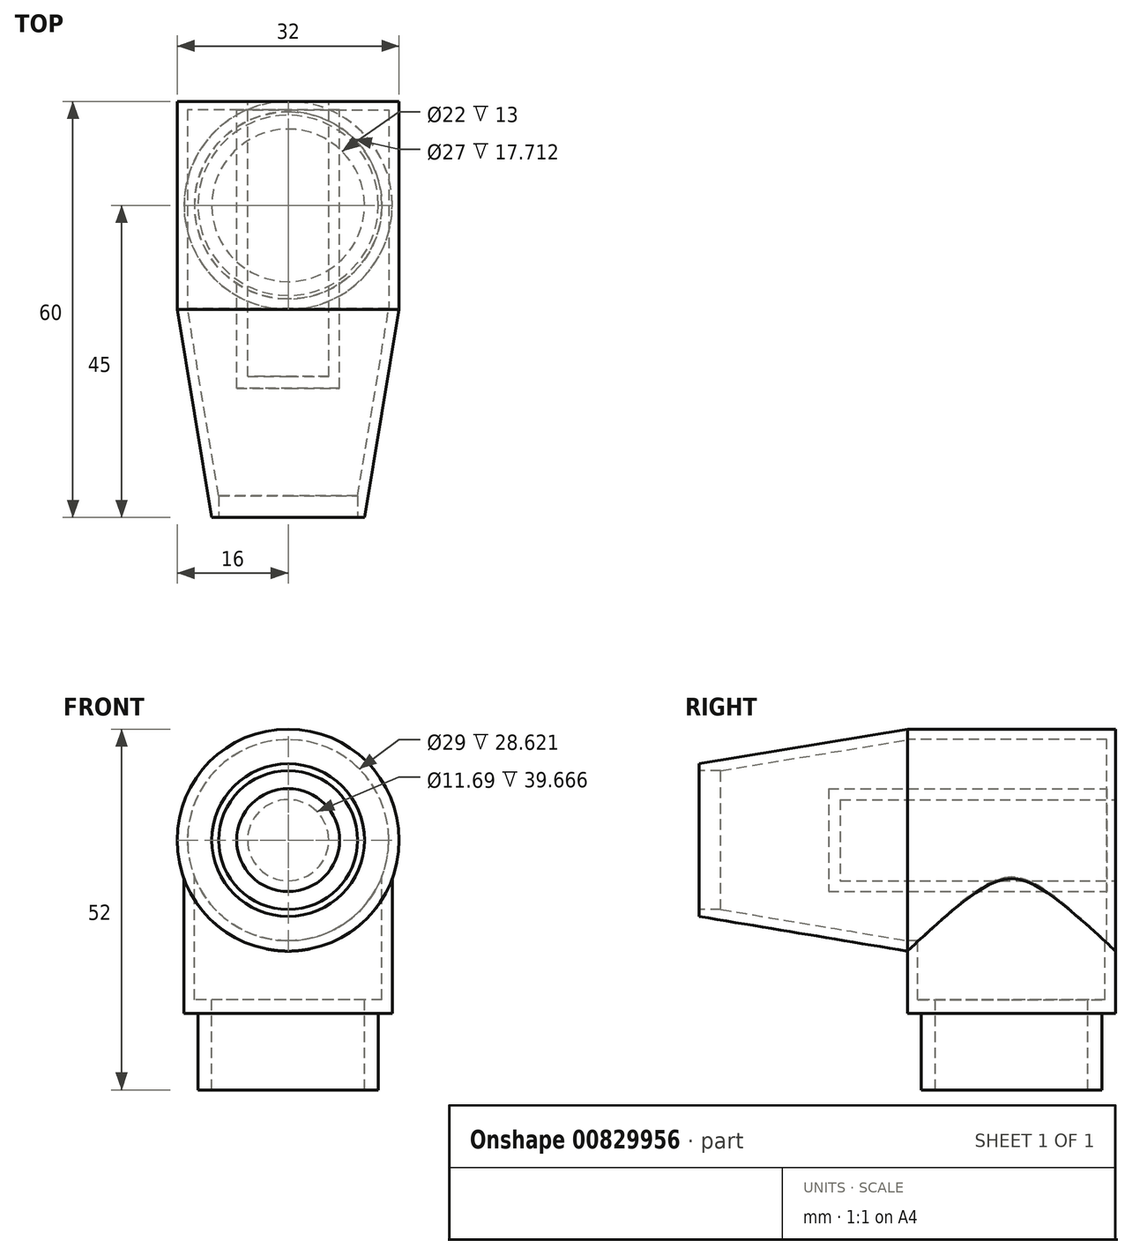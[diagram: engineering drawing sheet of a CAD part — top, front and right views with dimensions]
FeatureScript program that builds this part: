
annotation { "Feature Type Name" : "Feature", "Feature Type Description" : "" }
export const myFeature = defineFeature(function(context is Context, id is Id, definition is map)
    precondition{}
    {
        {
            var Q0;
            Q0=qCreatedBy(makeId("Right.planeOp"),FACE);
            var sketch = newSketch(context, id + "F0", { "sketchPlane" : qUnion([Q0])});
            skLineSegment(sketch, "E0", {"start": v(-38.09, 0) * mm, "end": v(40.8, 0) * mm, "construction": true});
            skLineSegment(sketch, "E1", {"start": v(0.12, 14.5) * mm, "end": v(30, 14.5) * mm});
            skLineSegment(sketch, "E2", {"start": v(30, 14.5) * mm, "end": v(30, 16) * mm});
            skLineSegment(sketch, "E3", {"start": v(30, 16) * mm, "end": v(0, 16) * mm});
            skLineSegment(sketch, "E4", {"start": v(0, 16) * mm, "end": v(-30, 11) * mm});
            skLineSegment(sketch, "E5", {"start": v(-30, 11) * mm, "end": v(-30, 10) * mm});
            skLineSegment(sketch, "E6", {"start": v(-26.88, 10) * mm, "end": v(0.12, 14.5) * mm});
            skLineSegment(sketch, "E7", {"start": v(-30, 10) * mm, "end": v(-26.88, 10) * mm});
            skSolve(sketch);
        }
        {
            var Q0;
            Q0 = qSketchRegion(id + "F0", true);
            var Q1;
            Q1=sQuery(id+"F0.wireOp",EDGE,"E0");
            revolve(context, id + "F1", {"surfaceOperationType" : NewSurfaceOperationType.NEW, "entities" : qUnion([Q0]), "axis" : qUnion([Q1]), "revolveType" : RevolveType.FULL});
        }
        {
            var Q0;
            Q0=qCreatedBy(makeId("Right.planeOp"),FACE);
            var sketch = newSketch(context, id + "F2", { "sketchPlane" : qUnion([Q0])});
            skLineSegment(sketch, "E8", {"start": v(15, 0) * mm, "end": v(15, -50.82) * mm, "construction": true});
            skLineSegment(sketch, "E9", {"start": v(0, 0) * mm, "end": v(0, -25) * mm});
            skLineSegment(sketch, "E10", {"start": v(0, -25) * mm, "end": v(2, -25) * mm});
            skLineSegment(sketch, "E11", {"start": v(2, -25) * mm, "end": v(2, -36) * mm});
            skLineSegment(sketch, "E12", {"start": v(2, -36) * mm, "end": v(4, -36) * mm});
            skLineSegment(sketch, "E13", {"start": v(4, -36) * mm, "end": v(4, -23) * mm});
            skLineSegment(sketch, "E14", {"start": v(4, -23) * mm, "end": v(1.5, -23) * mm});
            skLineSegment(sketch, "E15", {"start": v(1.5, -23) * mm, "end": v(1.5, 0) * mm});
            skLineSegment(sketch, "E16", {"start": v(1.5, 0) * mm, "end": v(0, 0) * mm});
            skSolve(sketch);
        }
        {
            var Q0;
            Q0 = qSketchRegion(id + "F2", true);
            var Q1;
            Q1=sQuery(id+"F2.wireOp",EDGE,"E8");
            revolve(context, id + "F3", {"operationType" : NewBodyOperationType.ADD, "surfaceOperationType" : NewSurfaceOperationType.NEW, "entities" : qUnion([Q0]), "axis" : qUnion([Q1]), "revolveType" : RevolveType.FULL});
        }
        {
            var Q0;
            Q0=qCreatedBy(makeId("Right.planeOp"),FACE);
            var sketch = newSketch(context, id + "F4", { "sketchPlane" : qUnion([Q0])});
            skLineSegment(sketch, "E17", {"start": v(0.12, 14.5) * mm, "end": v(30, 14.5) * mm});
            skLineSegment(sketch, "E18", {"start": v(-26.88, 10) * mm, "end": v(0.12, 14.5) * mm});
            skLineSegment(sketch, "E19", {"start": v(-30, 10) * mm, "end": v(-26.88, 10) * mm});
            skLineSegment(sketch, "E20", {"start": v(30, 14.5) * mm, "end": v(30, 0) * mm});
            skLineSegment(sketch, "E21", {"start": v(30, 0) * mm, "end": v(-30, 0) * mm});
            skLineSegment(sketch, "E22", {"start": v(-30, 0) * mm, "end": v(-30, 10) * mm});
            skSolve(sketch);
        }
        {
            var Q0;
            Q0=makeQuery(id+"F4.imprint","IMPRINT",FACE,{"disambiguationData":[TD([[makeQuery(id+"F4.imprint","IMPRINT",EDGE,{"derivedFrom":sQuery(id+"F4.wireOp",EDGE,"E17")}),-1.0]])]});
            var Q1;
            Q1=sQuery(id+"F4.wireOp",EDGE,"E21");
            revolve(context, id + "F5", {"operationType" : NewBodyOperationType.REMOVE, "surfaceOperationType" : NewSurfaceOperationType.NEW, "entities" : qUnion([Q0]), "axis" : qUnion([Q1]), "revolveType" : RevolveType.FULL, "oppositeDirection" : true});
        }
        {
            var Q0;
            Q0=qCreatedBy(makeId("Top.planeOp"),FACE);
            var sketch = newSketch(context, id + "F6", { "sketchPlane" : qUnion([Q0])});
            skCircle(sketch, "E23.0", {"center": v(0, 15) * mm, "radius": 13.5 * mm});
            skSolve(sketch);
        }
        {
            var Q0;
            Q0 = qSketchRegion(id + "F6", true);
            var Q1;
            Q1=makeQuery(id+"F3.boolean.opBoolean","SPLIT",FACE,{"disambiguationData":[TD([makeQuery(id+"F3.opRevolve","SWEPT_FACE",FACE,{"disambiguationData":[OSD([sQuery(id+"F2.wireOp",EDGE,"E15")])]})])],"derivedFrom":makeQuery(id+"F1.opRevolve","SWEPT_FACE",FACE,{"disambiguationData":[OSD([sQuery(id+"F0.wireOp",EDGE,"E3")])]})});
            extrude(context, id + "F7", {"entities" : qUnion([Q0]), "operationType" : NewBodyOperationType.REMOVE, "endBound" : BoundingType.UP_TO_SURFACE, "oppositeDirection" : true, "depth" : 25 * mm, "endBoundEntityFace" : qUnion([Q1]), "offsetDistance" : 25 * mm});
        }
        {
            var Q0;
            Q0=qCreatedBy(makeId("Right.planeOp"),FACE);
            var sketch = newSketch(context, id + "F8", { "sketchPlane" : qUnion([Q0])});
            skLineSegment(sketch, "E24", {"start": v(36.38, 0) * mm, "end": v(-20.22, 0) * mm, "construction": true});
            skLineSegment(sketch, "E25", {"start": v(30, 5.84) * mm, "end": v(30, 14.5) * mm});
            skLineSegment(sketch, "E26", {"start": v(30, 14.5) * mm, "end": v(28.75, 14.5) * mm});
            skLineSegment(sketch, "E27", {"start": v(28.75, 14.5) * mm, "end": v(28.75, 7.42) * mm});
            skLineSegment(sketch, "E28", {"start": v(28.75, 7.42) * mm, "end": v(-11.36, 7.42) * mm});
            skLineSegment(sketch, "E29", {"start": v(-11.36, 7.42) * mm, "end": v(-11.36, 0) * mm});
            skLineSegment(sketch, "E30", {"start": v(-11.36, 0) * mm, "end": v(-9.67, 0) * mm});
            skLineSegment(sketch, "E31", {"start": v(-9.67, 0) * mm, "end": v(-9.67, 5.84) * mm});
            skLineSegment(sketch, "E32", {"start": v(-9.67, 5.84) * mm, "end": v(30, 5.84) * mm});
            skLineSegment(sketch, "E33", {"start": v(0.12, 14.5) * mm, "end": v(30, 14.5) * mm, "construction": true});
            skSolve(sketch);
        }
        {
            var Q0;
            Q0=makeQuery(id+"F8.imprint","IMPRINT",FACE,{"disambiguationData":[TD([[makeQuery(id+"F8.imprint","IMPRINT",EDGE,{"derivedFrom":sQuery(id+"F8.wireOp",EDGE,"E25")}),1.0]])]});
            var Q1;
            Q1=sQuery(id+"F8.wireOp",EDGE,"E24");
            revolve(context, id + "F9", {"operationType" : NewBodyOperationType.ADD, "surfaceOperationType" : NewSurfaceOperationType.NEW, "entities" : qUnion([Q0]), "axis" : qUnion([Q1]), "revolveType" : RevolveType.FULL});
        }
    });
